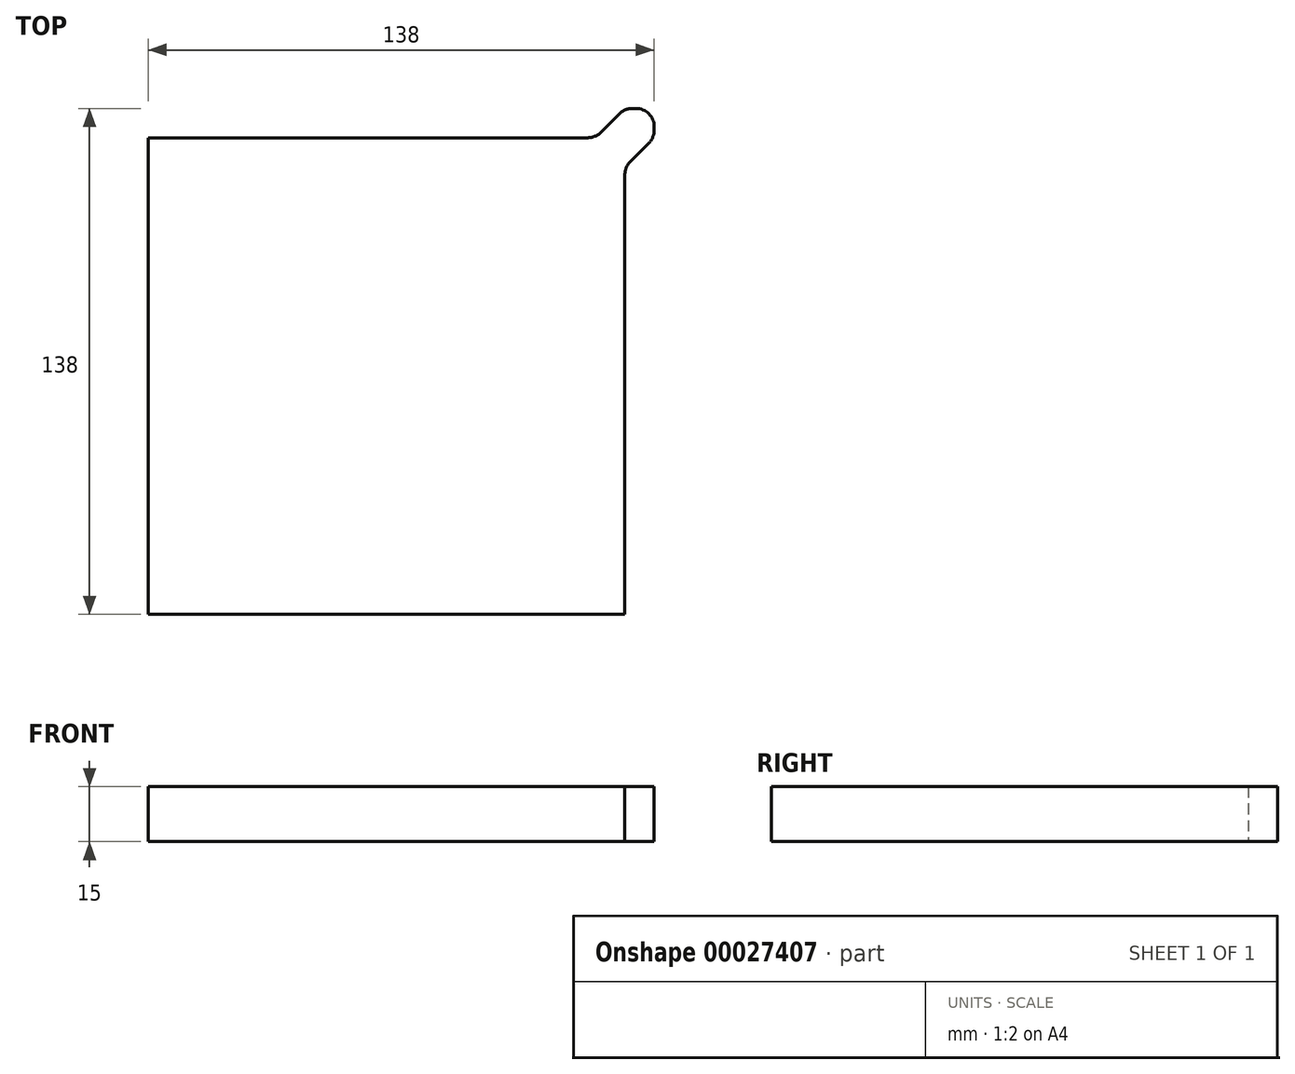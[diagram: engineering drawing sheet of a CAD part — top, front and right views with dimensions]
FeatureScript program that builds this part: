
annotation { "Feature Type Name" : "Feature", "Feature Type Description" : "" }
export const myFeature = defineFeature(function(context is Context, id is Id, definition is map)
    precondition{}
    {
        {
            var Q0;
            Q0=qCreatedBy(makeId("Top.planeOp"),FACE);
            var sketch = newSketch(context, id + "F0", { "sketchPlane" : qUnion([Q0])});
            skLineSegment(sketch, "E0.rect.bottom", {"start": v(57, 57) * mm, "end": v(-57, 57) * mm});
            skLineSegment(sketch, "E0.rect.top", {"start": v(57, -57) * mm, "end": v(-57, -57) * mm});
            skLineSegment(sketch, "E0.rect.left", {"start": v(57, 57) * mm, "end": v(57, -57) * mm});
            skLineSegment(sketch, "E0.rect.right", {"start": v(-57, 57) * mm, "end": v(-57, -57) * mm});
            skPoint(sketch, "E0.rect.middle", {"position": v(0, 0) * mm});
            skLineSegment(sketch, "E1.0", {"start": v(65, 65) * mm, "end": v(-65, 65) * mm});
            skLineSegment(sketch, "E1.1", {"start": v(65, 65) * mm, "end": v(65, -65) * mm});
            skLineSegment(sketch, "E1.2", {"start": v(65, -65) * mm, "end": v(-65, -65) * mm});
            skLineSegment(sketch, "E1.3", {"start": v(-65, 65) * mm, "end": v(-65, -65) * mm});
            skLineSegment(sketch, "E2.rect.bottom", {"start": v(57, 57) * mm, "end": v(65, 57) * mm});
            skLineSegment(sketch, "E2.rect.top", {"start": v(65, 73) * mm, "end": v(73, 73) * mm});
            skLineSegment(sketch, "E2.rect.left", {"start": v(57, 57) * mm, "end": v(57, 65) * mm});
            skPoint(sketch, "E2.rect.middle", {"position": v(65, 65) * mm});
            skLineSegment(sketch, "E3", {"start": v(73, 65) * mm, "end": v(65, 57) * mm});
            skLineSegment(sketch, "E4", {"start": v(65, 73) * mm, "end": v(57, 65) * mm});
            skLineSegment(sketch, "E5", {"start": v(73, 65) * mm, "end": v(73, 73) * mm});
            skPoint(sketch, "E6.end.orphan", {"position": v(73, 57) * mm});
            skPoint(sketch, "E7.orphan", {"position": v(57, 73) * mm});
            skSolve(sketch);
        }
        {
            var Q0;
            Q0=makeQuery(id+"F0.imprint","IMPRINT",FACE,{"disambiguationData":[TD([[makeQuery(id+"F0.imprint","IMPRINT",EDGE,{"derivedFrom":sQuery(id+"F0.wireOp",EDGE,"E0.rect.bottom")}),-1.0]])]});
            var Q1;
            Q1=makeQuery(id+"F0.imprint","IMPRINT",FACE,{"disambiguationData":[TD([[makeQuery(id+"F0.imprint","IMPRINT",EDGE,{"derivedFrom":sQuery(id+"F0.wireOp",EDGE,"E0.rect.bottom")}),1.0]])]});
            var Q2;
            {var subQ4=sQuery(id+"F0.wireOp",EDGE,"E2.rect.bottom");Q2=makeQuery(id+"F0.imprint","IMPRINT",FACE,{"disambiguationData":[TD([[makeQuery(id+"F0.imprint","IMPRINT",EDGE,{"derivedFrom":subQ4}),1.0]])]});}
            var Q3;
            Q3=makeQuery(id+"F0.imprint","IMPRINT",FACE,{"disambiguationData":[TD([[makeQuery(id+"F0.imprint","IMPRINT",EDGE,{"derivedFrom":sQuery(id+"F0.wireOp",EDGE,"E2.rect.top")}),-1.0]])]});
            extrude(context, id + "F1", {"entities" : qUnion([Q0, Q1, Q2, Q3]), "depth" : 15 * mm});
        }
        {
            var Q0;
            Q0=makeQuery(id+"F1.opExtrude","SWEPT_EDGE",EDGE,{"disambiguationData":[OSD([sQuery(id+"F0.wireOp",EDGE,"E3"),sQuery(id+"F0.wireOp",EDGE,"E5")])]});
            var Q1;
            Q1=makeQuery(id+"F1.opExtrude","SWEPT_EDGE",EDGE,{"disambiguationData":[OSD([sQuery(id+"F0.wireOp",EDGE,"E2.rect.top"),sQuery(id+"F0.wireOp",EDGE,"E5")])]});
            var Q2;
            Q2=makeQuery(id+"F1.opExtrude","SWEPT_EDGE",EDGE,{"disambiguationData":[OSD([sQuery(id+"F0.wireOp",EDGE,"E2.rect.top"),sQuery(id+"F0.wireOp",EDGE,"E4")])]});
            var Q3;
            Q3=makeQuery(id+"F1.opExtrude","SWEPT_EDGE",EDGE,{"disambiguationData":[OSD([sQuery(id+"F0.wireOp",EDGE,"E1.1"),sQuery(id+"F0.wireOp",EDGE,"E2.rect.bottom"),sQuery(id+"F0.wireOp",EDGE,"E3")])]});
            var Q4;
            Q4=makeQuery(id+"F1.opExtrude","SWEPT_EDGE",EDGE,{"disambiguationData":[OSD([sQuery(id+"F0.wireOp",EDGE,"E1.0"),sQuery(id+"F0.wireOp",EDGE,"E2.rect.left"),sQuery(id+"F0.wireOp",EDGE,"E4")])]});
            fillet(context, id + "F2", {"entities" : qUnion([Q0, Q1, Q2, Q3, Q4]), "radius" : 5 * mm, "tangentPropagation" : true, "allowEdgeOverflow" : false});
        }
    });
